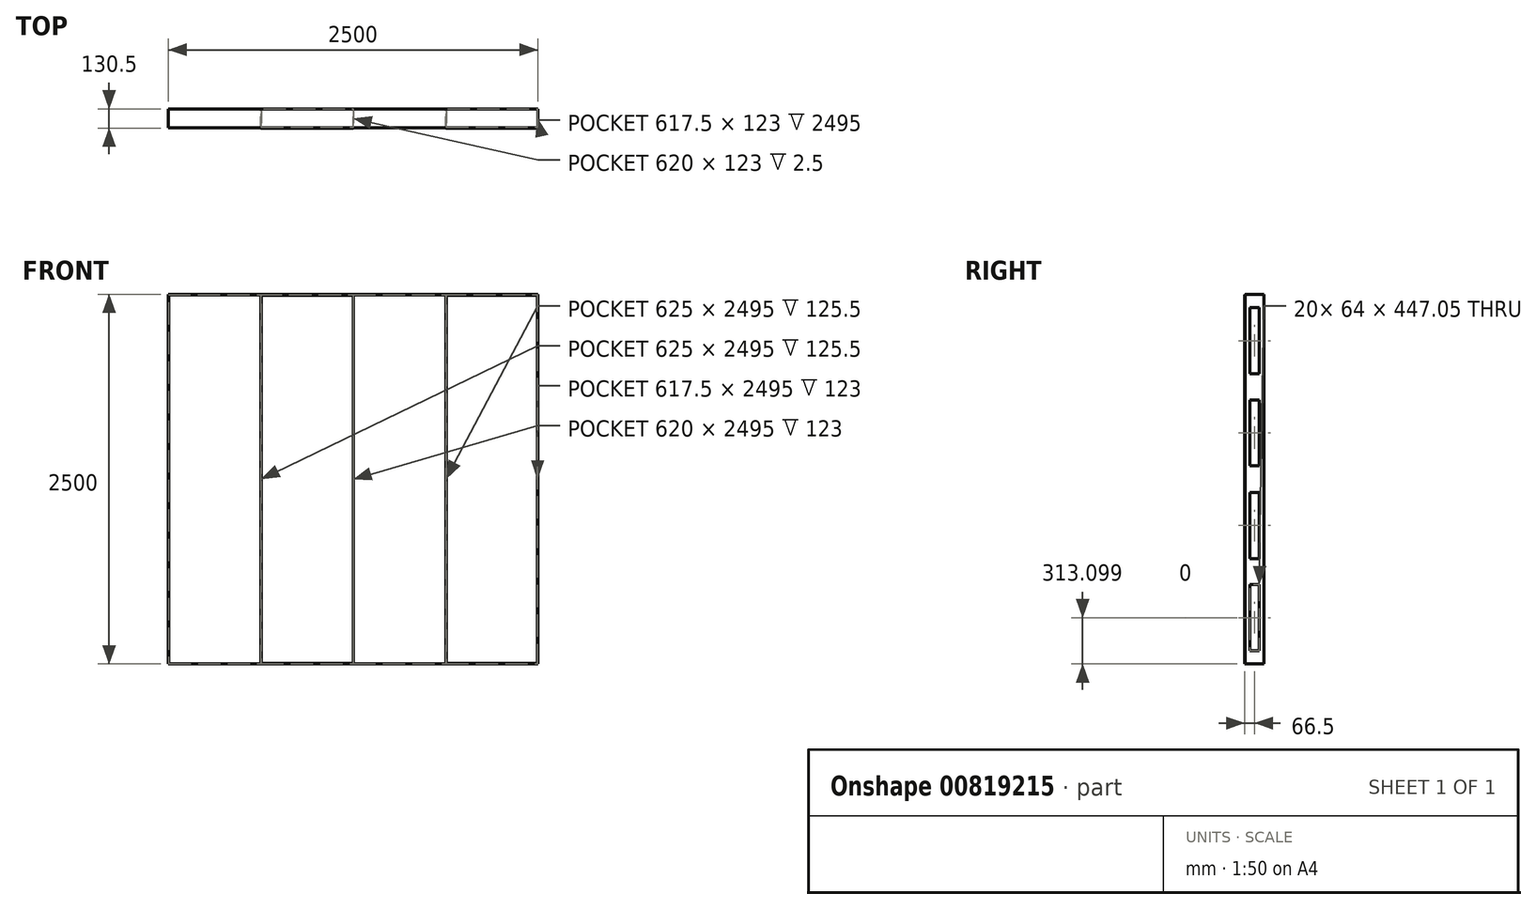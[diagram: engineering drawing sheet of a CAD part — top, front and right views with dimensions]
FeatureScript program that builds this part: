
annotation { "Feature Type Name" : "Feature", "Feature Type Description" : "" }
export const myFeature = defineFeature(function(context is Context, id is Id, definition is map)
    precondition{}
    {
        {
            var Q0;
            Q0=qCreatedBy(makeId("Front.planeOp"),FACE);
            var sketch = newSketch(context, id + "F0", { "sketchPlane" : qUnion([Q0])});
            skLineSegment(sketch, "E0.bottom", {"start": v(-1258.94, 1444.16) * mm, "end": v(1241.06, 1444.16) * mm});
            skLineSegment(sketch, "E0.top", {"start": v(-1258.94, -1055.84) * mm, "end": v(1241.06, -1055.84) * mm});
            skLineSegment(sketch, "E0.left", {"start": v(-1258.94, 1444.16) * mm, "end": v(-1258.94, -1055.84) * mm});
            skLineSegment(sketch, "E0.right", {"start": v(1241.06, 1444.16) * mm, "end": v(1241.06, -1055.84) * mm});
            skLineSegment(sketch, "E1.1.0.0", {"start": v(-8.94, 1444.16) * mm, "end": v(-8.94, -1055.84) * mm});
            skLineSegment(sketch, "E1.direction1", {"start": v(-1258.94, -1055.84) * mm, "end": v(-8.94, -1055.84) * mm, "construction": true});
            skLineSegment(sketch, "E2.1.0.0", {"start": v(-633.94, 1444.16) * mm, "end": v(-633.94, -1055.84) * mm});
            skLineSegment(sketch, "E2.3.0.0", {"start": v(616.06, 1444.16) * mm, "end": v(616.06, -1055.84) * mm});
            skLineSegment(sketch, "E2.direction1", {"start": v(-1258.94, -1055.84) * mm, "end": v(-633.94, -1055.84) * mm, "construction": true});
            skSolve(sketch);
        }
        {
            var Q0;
            {var subQ0=sQuery(id+"F0.wireOp",EDGE,"E2.1.0.0");Q0=makeQuery(id+"F0.imprint","IMPRINT",FACE,{"disambiguationData":[TD([[makeQuery(id+"F0.imprint","IMPRINT",EDGE,{"derivedFrom":subQ0}),1.0]])]});}
            var Q1;
            {var subQ0=sQuery(id+"F0.wireOp",EDGE,"E0.left");Q1=makeQuery(id+"F0.imprint","IMPRINT",FACE,{"disambiguationData":[TD([[makeQuery(id+"F0.imprint","IMPRINT",EDGE,{"derivedFrom":subQ0}),1.0]])]});}
            var Q2;
            {var subQ0=sQuery(id+"F0.wireOp",EDGE,"E1.1.0.0");Q2=makeQuery(id+"F0.imprint","IMPRINT",FACE,{"disambiguationData":[TD([[makeQuery(id+"F0.imprint","IMPRINT",EDGE,{"derivedFrom":subQ0}),1.0]])]});}
            var Q3;
            {var subQ2=sQuery(id+"F0.wireOp",EDGE,"E2.3.0.0");Q3=makeQuery(id+"F0.imprint","IMPRINT",FACE,{"disambiguationData":[TD([[makeQuery(id+"F0.imprint","IMPRINT",EDGE,{"derivedFrom":subQ2}),1.0]])]});}
            extrude(context, id + "F1", {"entities" : qUnion([Q0, Q1, Q2, Q3]), "depth" : 128 * mm, "offsetDistance" : 25 * mm});
        }
        {
            var Q0;
            Q0=makeQuery(id+"F1.opExtrude","CAP_FACE",FACE,{"disambiguationData":[OSD([sQuery(id+"F0.wireOp",EDGE,"E0.bottom"),sQuery(id+"F0.wireOp",EDGE,"E0.top"),sQuery(id+"F0.wireOp",EDGE,"E0.left"),sQuery(id+"F0.wireOp",EDGE,"E0.right")])],"isStart":false});
            shell(context, id + "F2", {"entities" : qUnion([Q0]), "thickness" : 2.5 * mm});
        }
        {
            var Q0;
            Q0=makeQuery(id+"F2.opShell","OFFSET_FACE",FACE,{"disambiguationData":[OSD([sQuery(id+"F0.wireOp",EDGE,"E0.bottom"),sQuery(id+"F0.wireOp",EDGE,"E0.top"),sQuery(id+"F0.wireOp",EDGE,"E0.left"),sQuery(id+"F0.wireOp",EDGE,"E0.right")])]});
            var sketch = newSketch(context, id + "F3", { "sketchPlane" : qUnion([Q0])});
            skLineSegment(sketch, "E3.bottom", {"start": v(-1256.44, 1441.66) * mm, "end": v(1238.56, 1441.66) * mm});
            skLineSegment(sketch, "E3.top", {"start": v(-1256.44, -1053.34) * mm, "end": v(1238.56, -1053.34) * mm});
            skLineSegment(sketch, "E3.left", {"start": v(-1256.44, 1441.66) * mm, "end": v(-1256.44, -1053.34) * mm});
            skLineSegment(sketch, "E3.right", {"start": v(1238.56, 1441.66) * mm, "end": v(1238.56, -1053.34) * mm});
            skLineSegment(sketch, "E4.1.0.0", {"start": v(-631.44, 1441.66) * mm, "end": v(-631.44, -1053.34) * mm});
            skLineSegment(sketch, "E4.2.0.0", {"start": v(-6.44, 1441.66) * mm, "end": v(-6.44, -1053.34) * mm});
            skLineSegment(sketch, "E4.3.0.0", {"start": v(618.56, 1441.66) * mm, "end": v(618.56, -1053.34) * mm});
            skLineSegment(sketch, "E4.4.0.0", {"start": v(1243.56, 1441.66) * mm, "end": v(1243.56, -1053.34) * mm});
            skLineSegment(sketch, "E4.direction1", {"start": v(-1256.44, -1053.34) * mm, "end": v(-631.44, -1053.34) * mm, "construction": true});
            skSolve(sketch);
        }
        {
            var Q0;
            {var subQ0=sQuery(id+"F3.wireOp",EDGE,"E4.1.0.0");Q0=makeQuery(id+"F3.imprint","IMPRINT",FACE,{"disambiguationData":[TD([[makeQuery(id+"F3.imprint","IMPRINT",EDGE,{"derivedFrom":subQ0}),1.0]])]});}
            var Q1;
            {var subQ0=sQuery(id+"F3.wireOp",EDGE,"E3.right");Q1=makeQuery(id+"F3.imprint","IMPRINT",FACE,{"disambiguationData":[TD([[makeQuery(id+"F3.imprint","IMPRINT",EDGE,{"derivedFrom":subQ0}),-1.0]])]});}
            extrude(context, id + "F4", {"entities" : qUnion([Q0, Q1]), "operationType" : NewBodyOperationType.ADD, "depth" : 128 * mm, "offsetDistance" : 25 * mm});
        }
        {
            var Q0;
            Q0=makeQuery(id+"F4.opExtrude","CAP_FACE",FACE,{"disambiguationData":[OSD([sQuery(id+"F3.wireOp",EDGE,"E3.bottom"),sQuery(id+"F3.wireOp",EDGE,"E3.top"),sQuery(id+"F3.wireOp",EDGE,"E4.1.0.0"),sQuery(id+"F3.wireOp",EDGE,"E4.2.0.0")])],"isStart":false});
            var Q1;
            Q1=makeQuery(id+"F4.opExtrude","CAP_FACE",FACE,{"disambiguationData":[OSD([sQuery(id+"F3.wireOp",EDGE,"E3.bottom"),sQuery(id+"F3.wireOp",EDGE,"E3.top"),sQuery(id+"F3.wireOp",EDGE,"E3.right"),sQuery(id+"F3.wireOp",EDGE,"E4.3.0.0")])],"isStart":false});
            shell(context, id + "F5", {"entities" : qUnion([Q0, Q1]), "thickness" : 2.5 * mm});
        }
        {
            var Q0;
            Q0=makeQuery(id+"F1.opExtrude","SWEPT_FACE",FACE,{"disambiguationData":[OSD([sQuery(id+"F0.wireOp",EDGE,"E0.left")])]});
            var sketch = newSketch(context, id + "F6", { "sketchPlane" : qUnion([Q0])});
            skLineSegment(sketch, "E5.bottom", {"start": v(0, 1444.16) * mm, "end": v(128, 1444.16) * mm});
            skLineSegment(sketch, "E5.top", {"start": v(0, 819.16) * mm, "end": v(128, 819.16) * mm});
            skLineSegment(sketch, "E5.left", {"start": v(0, 1444.16) * mm, "end": v(0, 819.16) * mm});
            skLineSegment(sketch, "E5.right", {"start": v(128, 1444.16) * mm, "end": v(128, 819.16) * mm});
            skLineSegment(sketch, "E6.bottom", {"start": v(96, 1354.58) * mm, "end": v(32, 1354.58) * mm});
            skLineSegment(sketch, "E6.top", {"start": v(96, 907.52) * mm, "end": v(32, 907.52) * mm});
            skLineSegment(sketch, "E6.left", {"start": v(96, 1354.58) * mm, "end": v(96, 907.52) * mm});
            skLineSegment(sketch, "E6.right", {"start": v(32, 1354.58) * mm, "end": v(32, 907.52) * mm});
            skPoint(sketch, "E6.middle", {"position": v(64, 1131.05) * mm});
            skLineSegment(sketch, "E7.MirrorCS", {"start": v(96, 730.79) * mm, "end": v(32, 730.79) * mm});
            skLineSegment(sketch, "E8.MirrorCS", {"start": v(96, 283.73) * mm, "end": v(32, 283.73) * mm});
            skLineSegment(sketch, "E9.MirrorCS", {"start": v(96, 283.73) * mm, "end": v(96, 730.79) * mm});
            skPoint(sketch, "E10.MirrorP", {"position": v(64, 507.26) * mm});
            skLineSegment(sketch, "E11.MirrorCS", {"start": v(0, 194.16) * mm, "end": v(128, 194.16) * mm});
            skLineSegment(sketch, "E12.MirrorCS", {"start": v(0, 194.16) * mm, "end": v(0, 819.16) * mm});
            skLineSegment(sketch, "E13.MirrorCS", {"start": v(128, 194.16) * mm, "end": v(128, 819.16) * mm});
            skLineSegment(sketch, "E14.MirrorCS", {"start": v(32, 283.73) * mm, "end": v(32, 730.79) * mm});
            skLineSegment(sketch, "E15.MirrorCS", {"start": v(96, -519.21) * mm, "end": v(32, -519.21) * mm});
            skLineSegment(sketch, "E16.MirrorCS", {"start": v(96, -342.48) * mm, "end": v(32, -342.48) * mm});
            skLineSegment(sketch, "E17.MirrorCS", {"start": v(96, -966.27) * mm, "end": v(32, -966.27) * mm});
            skLineSegment(sketch, "E18.MirrorCS", {"start": v(96, 104.58) * mm, "end": v(32, 104.58) * mm});
            skLineSegment(sketch, "E19.MirrorCS", {"start": v(96, 104.58) * mm, "end": v(96, -342.48) * mm});
            skLineSegment(sketch, "E20.MirrorCS", {"start": v(96, -966.27) * mm, "end": v(96, -519.21) * mm});
            skLineSegment(sketch, "E21.MirrorCS", {"start": v(0, -1055.84) * mm, "end": v(128, -1055.84) * mm});
            skLineSegment(sketch, "E22.MirrorCS", {"start": v(32, -966.27) * mm, "end": v(32, -519.21) * mm});
            skLineSegment(sketch, "E23.MirrorCS", {"start": v(0, 194.16) * mm, "end": v(0, -430.84) * mm});
            skPoint(sketch, "E24.MirrorP", {"position": v(64, -118.95) * mm});
            skLineSegment(sketch, "E25.MirrorCS", {"start": v(0, -1055.84) * mm, "end": v(0, -430.84) * mm});
            skLineSegment(sketch, "E26.MirrorCS", {"start": v(32, 104.58) * mm, "end": v(32, -342.48) * mm});
            skLineSegment(sketch, "E27.MirrorCS", {"start": v(128, -1055.84) * mm, "end": v(128, -430.84) * mm});
            skLineSegment(sketch, "E28.MirrorCS", {"start": v(0, -430.84) * mm, "end": v(128, -430.84) * mm});
            skPoint(sketch, "E29.MirrorP", {"position": v(64, -742.74) * mm});
            skLineSegment(sketch, "E30.MirrorCS", {"start": v(128, 194.16) * mm, "end": v(128, -430.84) * mm});
            skSolve(sketch);
        }
        {
            var Q0;
            Q0=makeQuery(id+"F6.imprint","IMPRINT",FACE,{"disambiguationData":[TD([[makeQuery(id+"F6.imprint","IMPRINT",EDGE,{"derivedFrom":sQuery(id+"F6.wireOp",EDGE,"E6.bottom")}),1.0]])]});
            var Q1;
            Q1=makeQuery(id+"F6.imprint","IMPRINT",FACE,{"disambiguationData":[TD([[makeQuery(id+"F6.imprint","IMPRINT",EDGE,{"derivedFrom":sQuery(id+"F6.wireOp",EDGE,"E7.MirrorCS")}),1.0]])]});
            var Q2;
            Q2=makeQuery(id+"F6.imprint","IMPRINT",FACE,{"disambiguationData":[TD([[makeQuery(id+"F6.imprint","IMPRINT",EDGE,{"derivedFrom":sQuery(id+"F6.wireOp",EDGE,"E16.MirrorCS")}),-1.0]])]});
            var Q3;
            Q3=makeQuery(id+"F6.imprint","IMPRINT",FACE,{"disambiguationData":[TD([[makeQuery(id+"F6.imprint","IMPRINT",EDGE,{"derivedFrom":sQuery(id+"F6.wireOp",EDGE,"E15.MirrorCS")}),1.0]])]});
            extrude(context, id + "F7", {"entities" : qUnion([Q0, Q1, Q2, Q3]), "operationType" : NewBodyOperationType.REMOVE, "endBound" : BoundingType.THROUGH_ALL, "oppositeDirection" : true, "depth" : 25 * mm, "offsetDistance" : 25 * mm});
        }
    });
